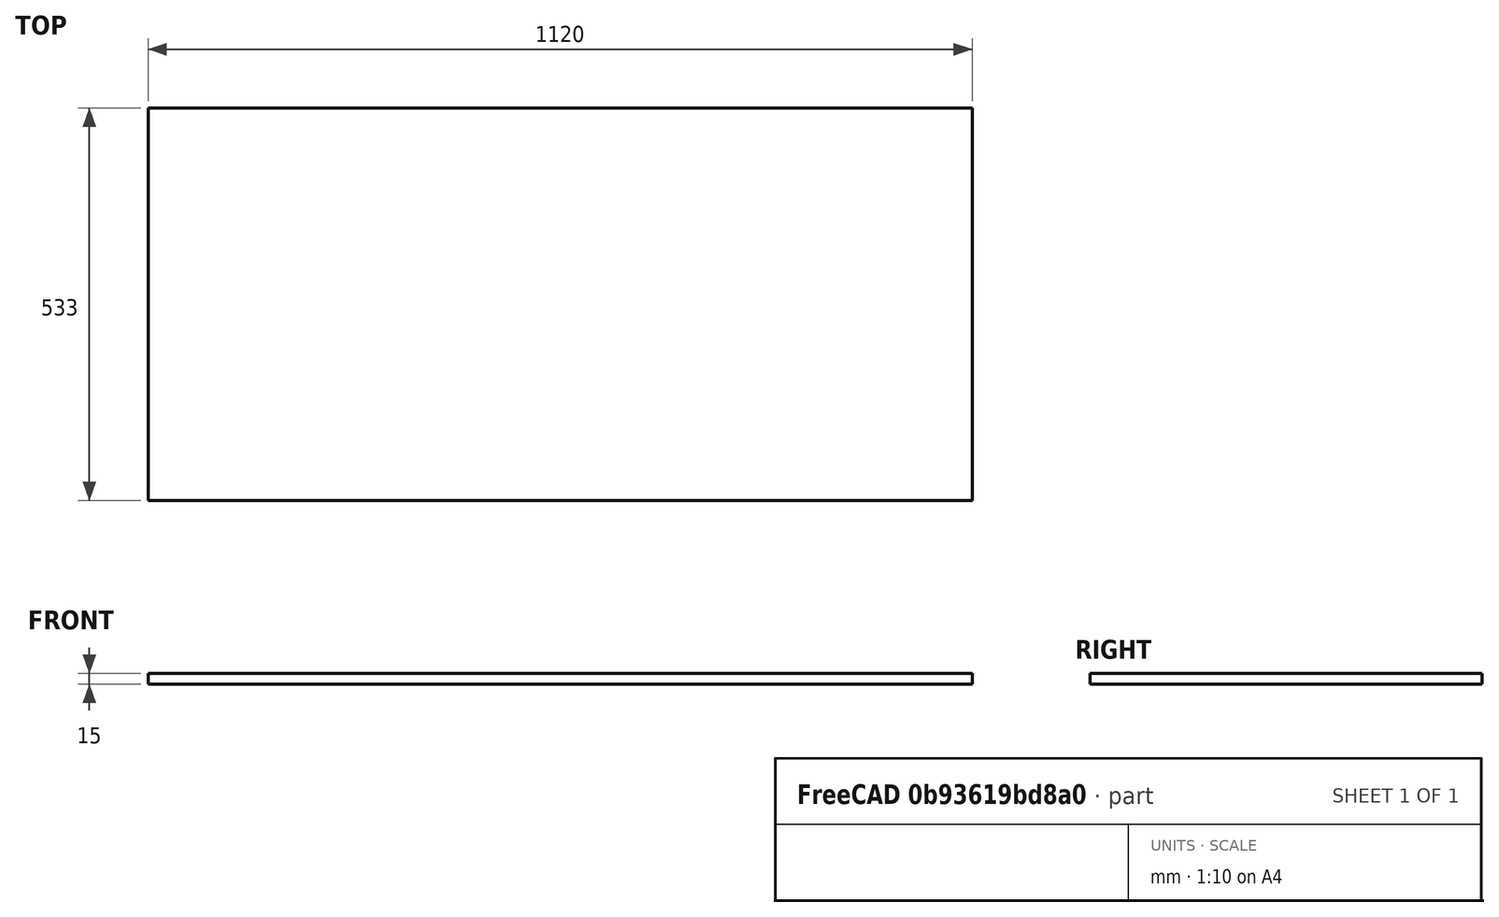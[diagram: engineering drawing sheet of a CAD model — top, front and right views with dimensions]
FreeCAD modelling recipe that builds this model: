
FCSTD DOCUMENT  (FreeCAD 0.17R13528 (Git))
Label: FondBoisPartieSuperieure
License: All rights reserved
LicenseURL: http://en.wikipedia.org/wiki/All_rights_reserved
objects: Drawing::FeatureViewPart×3, Drawing::FeatureViewPython×3, Part::Box×1, Drawing::FeaturePage×1
note: 1 computed .brp shape members not serialized (recipe doc carries the construction recipe); baked Part::Feature solids carry a one-line shape summary decoded from their .brp

FEATURE [Part::Box] Box  label="Cube"
  AttacherType = Attacher::AttachEngine3D
  Height = 15
  Length = 1120
  Width = 533
FEATURE [Drawing::FeatureViewPart] Ortho  label="Ortho_0_0"
  Direction = (0,0,1)
  HiddenWidth = 0.15
  LineWidth = 0.35
  Rotation = 0
  Scale = 0.15
  ShowHiddenLines = false
  ShowSmoothLines = false
  Source = -> Box
  Tolerance = 0.05
  ViewResult = <g id="Ortho_0_0"\n   transform="rotate(0,41.0417,140.829) translate(41.0417,140.829) scale(0.15,0.15)"\n  >\n<g   fill="none"\n   stroke="rgb(0, 0, 0)"\n   stroke-linecap="butt"\n   stroke-linejoin="miter"\n   stroke-width="2.333333"\n   transform="scale(1,-1)"\n  >\n<path id= "1" d=" M 0 0 L 0 533 " />\n<path id= "2" d=" M 1120 0 L 1120 533 " />\n<path id= "3" d=" M 0 0 L 1120 0 " />\n<path id= "4" d=" M 0 533 L 1120 533 " />\n</g>\n</g>
  Visible = false
  X = 41.0417
  Y = 140.829
FEATURE [Drawing::FeatureViewPart] Ortho001  label="Ortho_1_0"
  Direction = (-1,0,0)
  HiddenWidth = 0.15
  LineWidth = 0.35
  Rotation = 180
  Scale = 0.15
  ShowHiddenLines = false
  ShowSmoothLines = false
  Source = -> Box
  Tolerance = 0.05
  ViewResult = <g id="Ortho_1_0"\n   transform="rotate(180,239.896,140.829) translate(239.896,140.829) scale(0.15,0.15)"\n  >\n<g   fill="none"\n   stroke="rgb(0, 0, 0)"\n   stroke-linecap="butt"\n   stroke-linejoin="miter"\n   stroke-width="2.333333"\n   transform="scale(1,-1)"\n  >\n<path id= "1" d=" M 0 0 L -15 0 " />\n<path id= "2" d=" M -15 0 L -15 -533 " />\n<path id= "3" d=" M 0 -533 L -15 -533 " />\n<path id= "4" d=" M 0 0 L 0 -533 " />\n</g>\n</g>
  Visible = false
  X = 239.896
  Y = 140.829
FEATURE [Drawing::FeatureViewPart] Ortho002  label="Ortho_0_1"
  Direction = (0,-1,0)
  HiddenWidth = 0.15
  LineWidth = 0.35
  Rotation = 90
  Scale = 0.15
  ShowHiddenLines = false
  ShowSmoothLines = false
  Source = -> Box
  Tolerance = 0.05
  ViewResult = <g id="Ortho_0_1"\n   transform="rotate(90,41.0417,39.8958) translate(41.0417,39.8958) scale(0.15,0.15)"\n  >\n<g   fill="none"\n   stroke="rgb(0, 0, 0)"\n   stroke-linecap="butt"\n   stroke-linejoin="miter"\n   stroke-width="2.333333"\n   transform="scale(1,-1)"\n  >\n<path id= "1" d=" M 0 0 L -15 0 " />\n<path id= "2" d=" M 0 1120 L -15 1120 " />\n<path id= "3" d=" M 0 0 L 0 1120 " />\n<path id= "4" d=" M -15 0 L -15 1120 " />\n</g>\n</g>
  Visible = false
  X = 41.0417
  Y = 39.8958
FEATURE [Drawing::FeatureViewPython] dim001  # drawing view (typed FeaturePython)
  Rotation = 0
  ViewResult = <g> \n  <line x1="39.041700" y1="140.829000" x2="24.000000" y2="140.829000" style="stroke:rgb(0,0,255);stroke-width:0.30" />\n<line x1="39.041700" y1="60.879000" x2="24.000000" y2="60.879000" style="stroke:rgb(0,0,255);stroke-width:0.30" />\n<line x1="25.000000" y1="140.829000" x2="25.000000" y2="60.879000" style="stroke:rgb(0,0,255);stroke-width:0.30" /> \n  <polygon points="25.000000,60.879000 24.000000,63.879000 25.000000,64.879000 26.000000,63.879000" style="fill:rgb(0,0,255);stroke:rgb(0,0,255);stroke-width:0" /><polygon points="25.000000,140.829000 26.000000,137.829000 25.000000,136.829000 24.000000,137.829000" style="fill:rgb(0,0,255);stroke:rgb(0,0,255);stroke-width:0" /> \n  <text x="23.000000" y="100.854000" font-family="Verdana" font-size="3.6" fill="rgb(0,0,255)" text-anchor="middle" transform="rotate(-90.000000 23.000000,100.854000)" >533</text> </g>
  Visible = false
  X = 0
  Y = 0
  arrowL1 = 3
  arrowL2 = 1
  arrowW = 2
  arrow_scheme = 0
  autoPlaceOffset = 2
  autoPlaceText = true
  click1_x = 25
  click1_y = 85
  click2_x = 25
  click2_y = 85
  comma_decimal_place = false
  dimension_line_overshoot = 1
  gap_datum_points = 2
  halfDimension_linear = false
  lineColor = rgb(0,0,255)
  strokeWidth = 0.3
  textFormat_linear = %(value)3.0f
  textRenderer_color = rgb(0,0,255)
  textRenderer_family = Verdana
  textRenderer_size = 3.6
  unit_custom_scale = 1
  unit_scheme = 0
FEATURE [Drawing::FeatureViewPython] dim002  # drawing view (typed FeaturePython)
  Rotation = 0
  ViewResult = <g> \n  <line x1="41.041700" y1="142.829000" x2="41.041700" y2="151.000000" style="stroke:rgb(0,0,255);stroke-width:0.30" />\n<line x1="209.041700" y1="142.829000" x2="209.041700" y2="151.000000" style="stroke:rgb(0,0,255);stroke-width:0.30" />\n<line x1="41.041700" y1="150.000000" x2="209.041700" y2="150.000000" style="stroke:rgb(0,0,255);stroke-width:0.30" /> \n  <polygon points="209.041700,150.000000 206.041700,149.000000 205.041700,150.000000 206.041700,151.000000" style="fill:rgb(0,0,255);stroke:rgb(0,0,255);stroke-width:0" /><polygon points="41.041700,150.000000 44.041700,151.000000 45.041700,150.000000 44.041700,149.000000" style="fill:rgb(0,0,255);stroke:rgb(0,0,255);stroke-width:0" /> \n  <text x="125.041700" y="148.000000" font-family="Verdana" font-size="3.6" fill="rgb(0,0,255)" text-anchor="middle" transform="rotate(0.000000 125.041700,148.000000)" >1120</text> </g>
  Visible = false
  X = 0
  Y = 0
  arrowL1 = 3
  arrowL2 = 1
  arrowW = 2
  arrow_scheme = 0
  autoPlaceOffset = 2
  autoPlaceText = true
  click1_x = 120
  click1_y = 150
  click2_x = 120
  click2_y = 150
  comma_decimal_place = false
  dimension_line_overshoot = 1
  gap_datum_points = 2
  halfDimension_linear = false
  lineColor = rgb(0,0,255)
  strokeWidth = 0.3
  textFormat_linear = %(value)3.0f
  textRenderer_color = rgb(0,0,255)
  textRenderer_family = Verdana
  textRenderer_size = 3.6
  unit_custom_scale = 1
  unit_scheme = 0
FEATURE [Drawing::FeatureViewPython] dim003  # drawing view (typed FeaturePython)
  Rotation = 0
  ViewResult = <g> \n  <line x1="211.041700" y1="39.895800" x2="226.000000" y2="39.895800" style="stroke:rgb(0,0,255);stroke-width:0.30" />\n<line x1="211.041700" y1="37.195800" x2="226.000000" y2="37.195800" style="stroke:rgb(0,0,255);stroke-width:0.30" />\n<line x1="225.000000" y1="39.895800" x2="225.000000" y2="37.195800" style="stroke:rgb(0,0,255);stroke-width:0.30" /> \n  <polygon points="225.000000,37.195800 226.000000,34.195800 225.000000,33.195800 224.000000,34.195800" style="fill:rgb(0,0,255);stroke:rgb(0,0,255);stroke-width:0" /><polygon points="225.000000,39.895800 224.000000,42.895800 225.000000,43.895800 226.000000,42.895800" style="fill:rgb(0,0,255);stroke:rgb(0,0,255);stroke-width:0" /> \n  <text x="223.000000" y="38.545800" font-family="Verdana" font-size="3.6" fill="rgb(0,0,255)" text-anchor="middle" transform="rotate(-90.000000 223.000000,38.545800)" > 18</text> </g>
  Visible = false
  X = 0
  Y = 0
  arrowL1 = 3
  arrowL2 = 1
  arrowW = 2
  arrow_scheme = 0
  autoPlaceOffset = 2
  autoPlaceText = true
  click1_x = 225
  click1_y = 40.0208
  click2_x = 225
  click2_y = 40.0208
  comma_decimal_place = false
  dimension_line_overshoot = 1
  gap_datum_points = 2
  halfDimension_linear = false
  lineColor = rgb(0,0,255)
  strokeWidth = 0.3
  textFormat_linear = %(value)3.0f
  textRenderer_color = rgb(0,0,255)
  textRenderer_family = Verdana
  textRenderer_size = 3.6
  unit_custom_scale = 1
  unit_scheme = 0
FEATURE [Drawing::FeaturePage] Page
  EditableTexts = GB | Fond console | Contreplaqué okoumé | A4 | X / Y | 15/100 | PN | DN | DD/MM/YYYY | REV A
  Group = -> [Ortho,Ortho001,Ortho002,dim001,dim002,dim003]
  Template = <path>
note: 1 file-system path scrubbed to <path> (originals preserved in the JSON sidecar)
